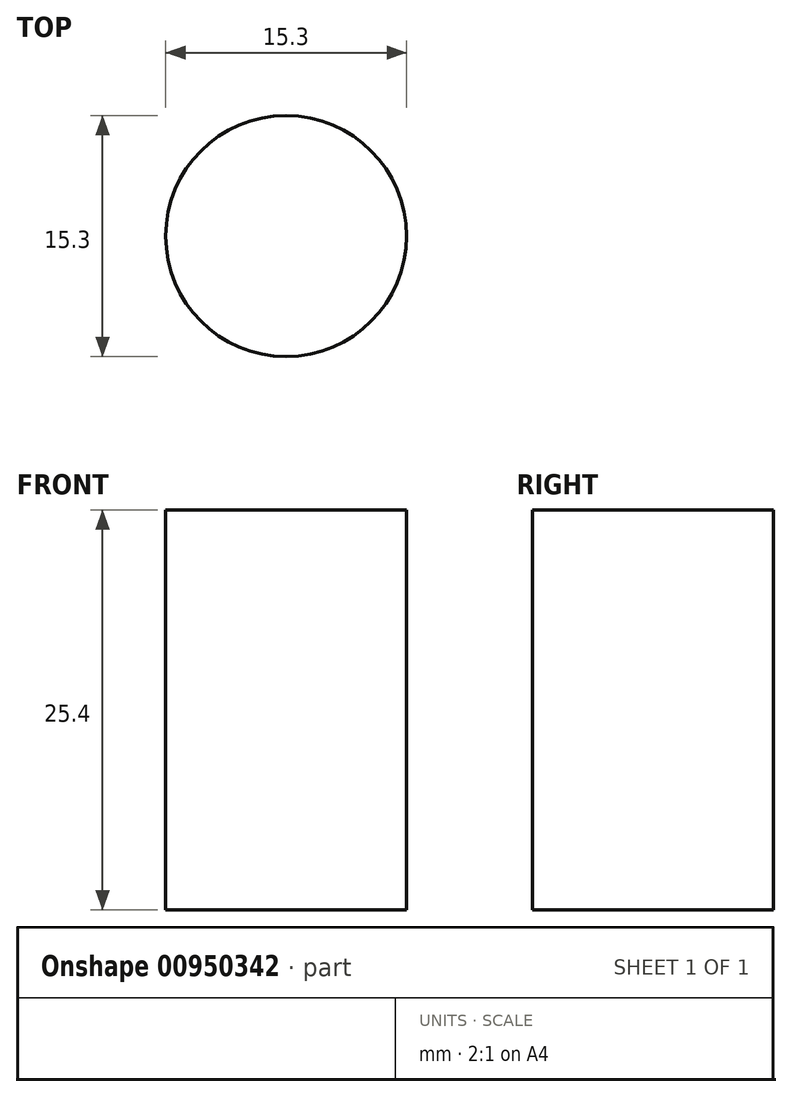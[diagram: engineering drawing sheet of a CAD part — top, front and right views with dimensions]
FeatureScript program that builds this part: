
annotation { "Feature Type Name" : "Feature", "Feature Type Description" : "" }
export const myFeature = defineFeature(function(context is Context, id is Id, definition is map)
    precondition{}
    {
        {
            var Q0;
            Q0=qCreatedBy(makeId("Top.planeOp"),FACE);
            var sketch = newSketch(context, id + "F0", { "sketchPlane" : qUnion([Q0])});
            skCircle(sketch, "E0", {"center": v(0, 0) * mm, "radius": 7.65 * mm});
            skSolve(sketch);
        }
        {
            var Q0;
            Q0=makeQuery(id+"F0.imprint","IMPRINT",FACE,{"disambiguationData":[TD([[makeQuery(id+"F0.imprint","IMPRINT",EDGE,{"derivedFrom":sQuery(id+"F0.wireOp",EDGE,"E0")}),1.0]])]});
            extrude(context, id + "F1", {"entities" : qUnion([Q0]), "depth" : 25.4 * mm, "offsetDistance" : 25.4 * mm});
        }
    });
